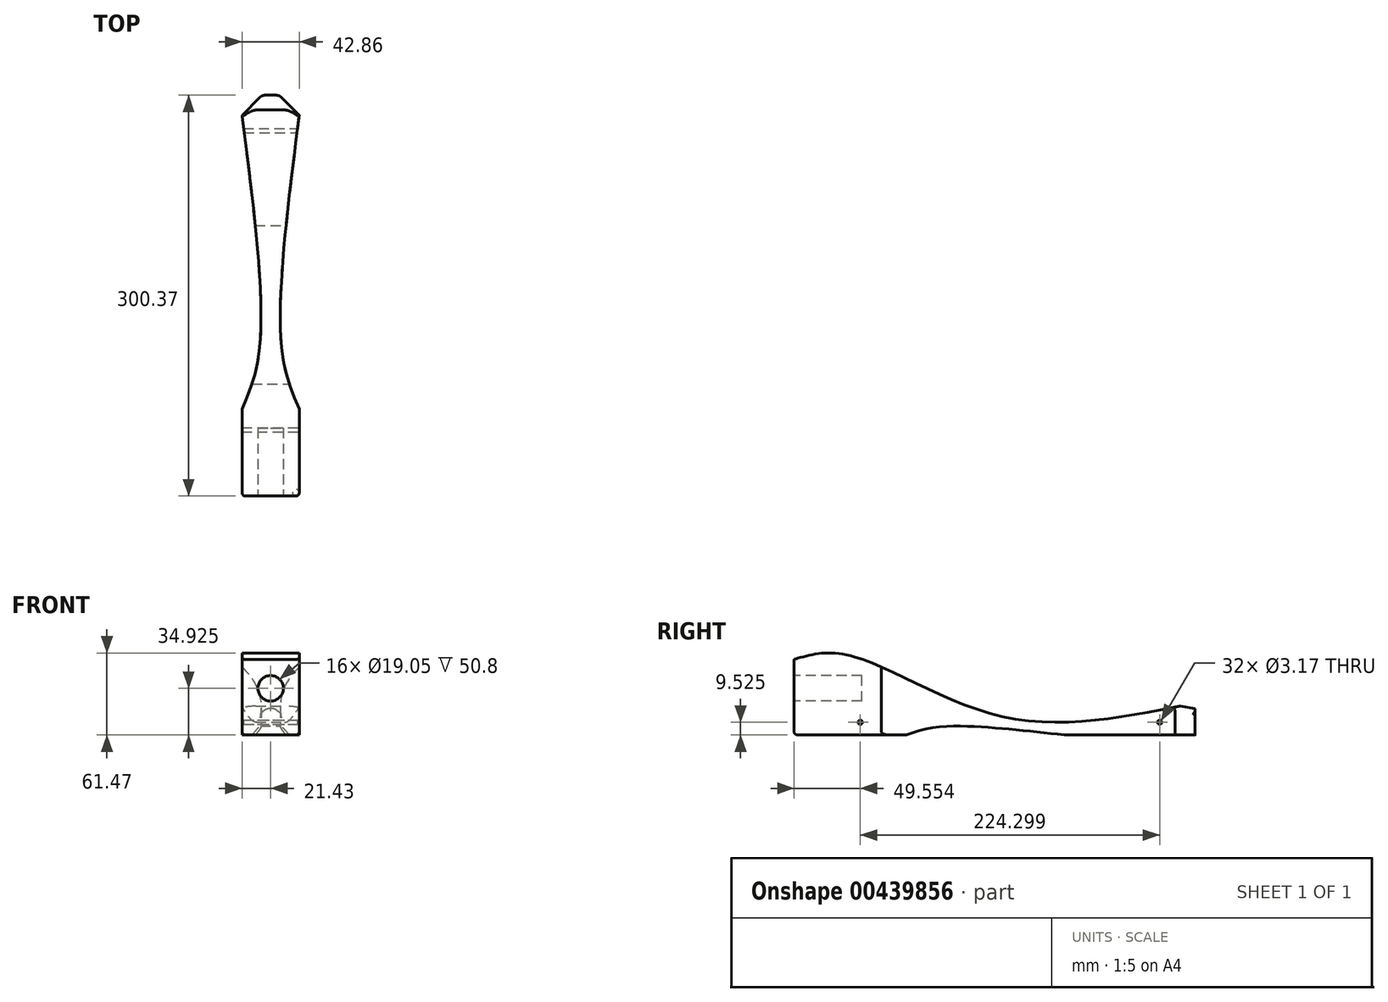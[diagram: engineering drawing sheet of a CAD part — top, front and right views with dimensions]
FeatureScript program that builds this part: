
annotation { "Feature Type Name" : "Feature", "Feature Type Description" : "" }
export const myFeature = defineFeature(function(context is Context, id is Id, definition is map)
    precondition{}
    {
        {
            var Q0;
            Q0=qCreatedBy(makeId("Right.planeOp"),FACE);
            var sketch = newSketch(context, id + "F0", { "sketchPlane" : qUnion([Q0])});
            skLineSegment(sketch, "E0", {"start": v(-152.4, 0) * mm, "end": v(152.4, 0) * mm});
            skLineSegment(sketch, "E1", {"start": v(-152.4, 0) * mm, "end": v(-152.4, 69.85) * mm});
            skLineSegment(sketch, "E2", {"start": v(152.4, 0) * mm, "end": v(152.4, 19.05) * mm});
            skLineSegment(sketch, "E3", {"start": v(152.4, 19.05) * mm, "end": v(-152.4, 69.85) * mm});
            skPoint(sketch, "E4.endSnap0", {"position": v(-152.4, 34.93) * mm});
            skLineSegment(sketch, "E5.0", {"start": v(-95.25, 50.8) * mm, "end": v(-152.4, 50.8) * mm, "construction": true});
            skLineSegment(sketch, "E5.1", {"start": v(-95.25, 50.8) * mm, "end": v(-95.25, 19.05) * mm, "construction": true});
            skLineSegment(sketch, "E5.2", {"start": v(-95.25, 19.05) * mm, "end": v(-152.4, 19.05) * mm, "construction": true});
            skSolve(sketch);
        }
        {
            var Q0;
            Q0=makeQuery(id+"F0.imprint","IMPRINT",FACE,{"disambiguationData":[TD([[makeQuery(id+"F0.imprint","IMPRINT",EDGE,{"derivedFrom":sQuery(id+"F0.wireOp",EDGE,"E0")}),1.0]])]});
            extrude(context, id + "F1", {"entities" : qUnion([Q0]), "depth" : 42.86 * mm, "symmetric" : true});
        }
        {
            var Q0;
            Q0=makeQuery(id+"F1.opExtrude","SWEPT_FACE",FACE,{"disambiguationData":[OSD([sQuery(id+"F0.wireOp",EDGE,"E1")])]});
            var sketch = newSketch(context, id + "F2", { "sketchPlane" : qUnion([Q0])});
            skLineSegment(sketch, "E6", {"start": v(21.43, 34.93) * mm, "end": v(0, 34.93) * mm, "construction": true});
            skCircle(sketch, "E7", {"center": v(0, 34.93) * mm, "radius": 9.53 * mm});
            skSolve(sketch);
        }
        {
            var Q0;
            Q0=makeQuery(id+"F2.imprint","IMPRINT",FACE,{"disambiguationData":[TD([[makeQuery(id+"F2.imprint","IMPRINT",EDGE,{"derivedFrom":sQuery(id+"F2.wireOp",EDGE,"E7")}),1.0]])]});
            var Q1;
            Q1=sQuery(id+"F2.wireOp",EDGE,"E7");
            extrude(context, id + "F3", {"entities" : qUnion([Q0]), "operationType" : NewBodyOperationType.REMOVE, "surfaceEntities" : qUnion([Q1]), "oppositeDirection" : true, "depth" : 50.8 * mm});
        }
        {
            var Q0;
            Q0=makeQuery(id+"F1.opExtrude","CAP_FACE",FACE,{"disambiguationData":[OSD([sQuery(id+"F0.wireOp",EDGE,"E0"),sQuery(id+"F0.wireOp",EDGE,"E1"),sQuery(id+"F0.wireOp",EDGE,"E2"),sQuery(id+"F0.wireOp",EDGE,"E3")])],"isStart":false});
            var sketch = newSketch(context, id + "F4", { "sketchPlane" : qUnion([Q0])});
            skLineSegment(sketch, "E8", {"start": v(-152.4, 34.93) * mm, "end": v(-152.4, 44.45) * mm, "construction": true});
            skLineSegment(sketch, "E9.0", {"start": v(-95.25, 19.05) * mm, "end": v(-152.4, 19.05) * mm, "construction": true});
            skLineSegment(sketch, "E9.1", {"start": v(-95.25, 50.8) * mm, "end": v(-95.25, 19.05) * mm, "construction": true});
            skLineSegment(sketch, "E9.2", {"start": v(-152.4, 50.8) * mm, "end": v(-95.25, 50.8) * mm, "construction": true});
            skLineSegment(sketch, "E10", {"start": v(57.15, 0) * mm, "end": v(57.15, 34.93) * mm, "construction": true});
            skLineSegment(sketch, "E11", {"start": v(-152.4, 44.45) * mm, "end": v(-101.6, 44.45) * mm, "construction": true});
            skLineSegment(sketch, "E12", {"start": v(-101.6, 44.45) * mm, "end": v(-101.6, 25.4) * mm, "construction": true});
            skLineSegment(sketch, "E13", {"start": v(-101.6, 25.4) * mm, "end": v(-152.4, 25.4) * mm, "construction": true});
            skFitSpline(sketch, "E14", {"points": [v(-152.4, 56.65) * mm, v(-111.85, 59.82) * mm, v(0, 14.63) * mm, v(136.83, 21.64) * mm], "startDerivative": vector(164.8, 47.68) * mm, "endDerivative": vector(342.19, 67.53) * mm});
            skLineSegment(sketch, "E15", {"start": v(-152.4, 56.65) * mm, "end": v(-152.4, 0) * mm});
            skLineSegment(sketch, "E16", {"start": v(-152.4, 0) * mm, "end": v(152.4, 0) * mm});
            skLineSegment(sketch, "E17", {"start": v(152.4, 0) * mm, "end": v(152.4, 19.05) * mm});
            skLineSegment(sketch, "E18", {"start": v(152.4, 19.05) * mm, "end": v(136.83, 21.64) * mm});
            skCircle(sketch, "E19", {"center": v(-102.85, 9.53) * mm, "radius": 1.59 * mm});
            skCircle(sketch, "E20", {"center": v(121.45, 9.53) * mm, "radius": 1.59 * mm});
            skFitSpline(sketch, "E21", {"points": [v(-68.4, 0) * mm, v(-42.6, 6.17) * mm, v(50.18, 0) * mm], "startDerivative": vector(62.26, 22.44) * mm, "endDerivative": vector(164.57, -18.32) * mm});
            skSolve(sketch);
        }
        {
            var Q0;
            Q0=makeQuery(id+"F1.opExtrude","SWEPT_FACE",FACE,{"disambiguationData":[OSD([sQuery(id+"F0.wireOp",EDGE,"E0")])]});
            var sketch = newSketch(context, id + "F5", { "sketchPlane" : qUnion([Q0])});
            skLineSegment(sketch, "E22", {"start": v(0, 152.4) * mm, "end": v(0, -152.4) * mm, "construction": true});
            skLineSegment(sketch, "E23", {"start": v(15.88, 152.4) * mm, "end": v(15.88, 95.25) * mm, "construction": true});
            skLineSegment(sketch, "E24", {"start": v(15.88, 95.25) * mm, "end": v(-15.87, 95.25) * mm, "construction": true});
            skLineSegment(sketch, "E25", {"start": v(-15.87, 95.25) * mm, "end": v(-15.87, 152.4) * mm, "construction": true});
            skLineSegment(sketch, "E26", {"start": v(0, 152.4) * mm, "end": v(-9.53, 152.4) * mm, "construction": true});
            skLineSegment(sketch, "E27", {"start": v(-9.53, 152.4) * mm, "end": v(-9.53, 101.6) * mm, "construction": true});
            skLineSegment(sketch, "E28", {"start": v(-9.52, 101.6) * mm, "end": v(9.53, 101.6) * mm, "construction": true});
            skLineSegment(sketch, "E29", {"start": v(9.53, 101.6) * mm, "end": v(9.53, 152.4) * mm, "construction": true});
            skLineSegment(sketch, "E30", {"start": v(0, -147.97) * mm, "end": v(-6.45, -147.97) * mm});
            skLineSegment(sketch, "E31", {"start": v(-6.45, -147.97) * mm, "end": v(-21.43, -132.9) * mm});
            skLineSegment(sketch, "E32.MirrorCS", {"start": v(0, -147.97) * mm, "end": v(6.45, -147.97) * mm});
            skLineSegment(sketch, "E33.MirrorCS", {"start": v(6.45, -147.97) * mm, "end": v(21.43, -132.9) * mm});
            skLineSegment(sketch, "E34", {"start": v(-21.43, -132.9) * mm, "end": v(-21.43, -152.4) * mm});
            skLineSegment(sketch, "E35", {"start": v(-21.43, -152.4) * mm, "end": v(21.43, -152.4) * mm});
            skLineSegment(sketch, "E36", {"start": v(21.43, -152.4) * mm, "end": v(21.43, -132.9) * mm});
            skLineSegment(sketch, "E37", {"start": v(-6.45, -147.97) * mm, "end": v(6.45, -147.97) * mm});
            skLineSegment(sketch, "E38", {"start": v(21.43, -132.9) * mm, "end": v(21.43, 152.4) * mm});
            skLineSegment(sketch, "E39", {"start": v(21.43, 152.4) * mm, "end": v(-21.43, 152.4) * mm});
            skLineSegment(sketch, "E40", {"start": v(-21.43, 152.4) * mm, "end": v(-21.43, -132.9) * mm});
            skFitSpline(sketch, "E41", {"points": [v(-21.43, 87.09) * mm, v(-8.22, 41.22) * mm, v(-21.43, -132.9) * mm], "startDerivative": vector(48.54, -111.02) * mm, "endDerivative": vector(-39.36, -308.36) * mm});
            skFitSpline(sketch, "E42.MirrorCS", {"points": [v(21.43, 87.09) * mm, v(8.22, 41.22) * mm, v(21.43, -132.9) * mm], "startDerivative": vector(-48.54, -111.02) * mm, "endDerivative": vector(39.36, -308.36) * mm});
            skSolve(sketch);
        }
        {
            var Q0;
            Q0=makeQuery(id+"F4.imprint","IMPRINT",FACE,{"disambiguationData":[TD([[makeQuery(id+"F4.imprint","IMPRINT",EDGE,{"derivedFrom":sQuery(id+"F4.wireOp",EDGE,"E14")}),-1.0]])]});
            extrude(context, id + "F6", {"entities" : qUnion([Q0]), "operationType" : NewBodyOperationType.INTERSECT, "endBound" : BoundingType.THROUGH_ALL, "oppositeDirection" : true, "depth" : 25.4 * mm});
        }
        {
            var Q0;
            Q0=makeQuery(id+"F5.imprint","IMPRINT",FACE,{"disambiguationData":[TD([[makeQuery(id+"F5.imprint","IMPRINT",EDGE,{"derivedFrom":sQuery(id+"F5.wireOp",EDGE,"E31")}),1.0]])]});
            extrude(context, id + "F7", {"entities" : qUnion([Q0]), "operationType" : NewBodyOperationType.REMOVE, "oppositeDirection" : true, "depth" : 25.4 * mm});
        }
        {
            var Q0;
            Q0=makeQuery(id+"F5.imprint","IMPRINT",FACE,{"disambiguationData":[TD([[makeQuery(id+"F5.imprint","IMPRINT",EDGE,{"derivedFrom":sQuery(id+"F5.wireOp",EDGE,"E31")}),-1.0]])]});
            extrude(context, id + "F8", {"entities" : qUnion([Q0]), "operationType" : NewBodyOperationType.INTERSECT, "endBound" : BoundingType.THROUGH_ALL, "oppositeDirection" : true, "depth" : 25.4 * mm});
        }
        {
            var Q0;
            Q0=makeQuery(id+"F7.boolean.opBoolean","INTERSECT",EDGE,{"derivedFrom":[makeQuery(id+"F1.opExtrude","SWEPT_FACE",FACE,{"disambiguationData":[OSD([sQuery(id+"F0.wireOp",EDGE,"E3")])]}),makeQuery(id+"F7.opExtrude","SWEPT_FACE",FACE,{"disambiguationData":[OSD([sQuery(id+"F5.wireOp",EDGE,"E31")])]})]});
            var Q1;
            Q1=makeQuery(id+"F7.boolean.opBoolean","INTERSECT",EDGE,{"derivedFrom":[makeQuery(id+"F1.opExtrude","SWEPT_FACE",FACE,{"disambiguationData":[OSD([sQuery(id+"F0.wireOp",EDGE,"E3")])]}),makeQuery(id+"F7.opExtrude","SWEPT_FACE",FACE,{"disambiguationData":[OSD([sQuery(id+"F5.wireOp",EDGE,"E33.MirrorCS")])]})]});
            var Q2;
            Q2=makeQuery(id+"F7.boolean.opBoolean","COPY",EDGE,{"derivedFrom":makeQuery(id+"F7.opExtrude","SWEPT_EDGE",EDGE,{"disambiguationData":[OSD([sQuery(id+"F5.wireOp",EDGE,"E31"),sQuery(id+"F5.wireOp",EDGE,"E37")])]})});
            var Q3;
            Q3=makeQuery(id+"F7.boolean.opBoolean","COPY",EDGE,{"derivedFrom":makeQuery(id+"F7.opExtrude","SWEPT_EDGE",EDGE,{"disambiguationData":[OSD([sQuery(id+"F5.wireOp",EDGE,"E33.MirrorCS"),sQuery(id+"F5.wireOp",EDGE,"E37")])]})});
            var Q4;
            {var subQ0=sQuery(id+"F5.wireOp",EDGE,"E42.MirrorCS");var subQ1=sQuery(id+"F5.wireOp",EDGE,"E38");var subQ2=sQuery(id+"F5.wireOp",EDGE,"E36");var subQ3=sQuery(id+"F5.wireOp",EDGE,"E33.MirrorCS");Q4=makeQuery(id+"F8.boolean.opBoolean","MERGE",EDGE,{"derivedFrom":[makeQuery(id+"F7.boolean.opBoolean","COPY",EDGE,{"derivedFrom":makeQuery(id+"F7.opExtrude","SWEPT_EDGE",EDGE,{"disambiguationData":[OSD([subQ3,subQ2,subQ1,subQ0])]})}),makeQuery(id+"F8.boolean.toolComplement.opBoolean","COPY",EDGE,{"derivedFrom":makeQuery(id+"F8.opExtrude","SWEPT_EDGE",EDGE,{"disambiguationData":[OSD([subQ3,subQ2,subQ1,subQ0])]})})]});}
            var Q5;
            Q5=makeQuery(id+"F7.boolean.opBoolean","COPY",EDGE,{"derivedFrom":makeQuery(id+"F7.opExtrude","CAP_EDGE",EDGE,{"disambiguationData":[OSD([sQuery(id+"F5.wireOp",EDGE,"E33.MirrorCS")])],"isStart":true})});
            var Q6;
            Q6=makeQuery(id+"F7.boolean.opBoolean","COPY",EDGE,{"derivedFrom":makeQuery(id+"F7.opExtrude","CAP_EDGE",EDGE,{"disambiguationData":[OSD([sQuery(id+"F5.wireOp",EDGE,"E37")])],"isStart":true})});
            var Q7;
            Q7=makeQuery(id+"F7.boolean.opBoolean","COPY",EDGE,{"derivedFrom":makeQuery(id+"F7.opExtrude","CAP_EDGE",EDGE,{"disambiguationData":[OSD([sQuery(id+"F5.wireOp",EDGE,"E31")])],"isStart":true})});
            var Q8;
            {var subQ0=sQuery(id+"F5.wireOp",EDGE,"E41");var subQ1=sQuery(id+"F5.wireOp",EDGE,"E40");var subQ2=sQuery(id+"F5.wireOp",EDGE,"E34");var subQ3=sQuery(id+"F5.wireOp",EDGE,"E31");Q8=makeQuery(id+"F8.boolean.opBoolean","MERGE",EDGE,{"derivedFrom":[makeQuery(id+"F7.boolean.opBoolean","COPY",EDGE,{"derivedFrom":makeQuery(id+"F7.opExtrude","SWEPT_EDGE",EDGE,{"disambiguationData":[OSD([subQ3,subQ2,subQ1,subQ0])]})}),makeQuery(id+"F8.boolean.toolComplement.opBoolean","COPY",EDGE,{"derivedFrom":makeQuery(id+"F8.opExtrude","SWEPT_EDGE",EDGE,{"disambiguationData":[OSD([subQ3,subQ2,subQ1,subQ0])]})})]});}
            fillet(context, id + "F9", {"entities" : qUnion([Q0, Q1, Q2, Q3, Q4, Q5, Q6, Q7, Q8]), "radius" : 5.08 * mm, "tangentPropagation" : true, "allowEdgeOverflow" : false});
        }
        {
            var Q0;
            Q0=makeQuery(id+"F8.boolean.opBoolean","INTERSECT",EDGE,{"derivedFrom":[makeQuery(id+"F6.boolean.opBoolean","COPY",FACE,{"derivedFrom":makeQuery(id+"F6.boolean.toolComplement.opBoolean","COPY",FACE,{"derivedFrom":makeQuery(id+"F6.opExtrude","SWEPT_FACE",FACE,{"disambiguationData":[OSD([sQuery(id+"F4.wireOp",EDGE,"E14")])]})})}),makeQuery(id+"F8.boolean.toolComplement.opBoolean","COPY",FACE,{"derivedFrom":makeQuery(id+"F8.opExtrude","SWEPT_FACE",FACE,{"disambiguationData":[OSD([sQuery(id+"F5.wireOp",EDGE,"E41")])]})})]});
            var Q1;
            Q1=makeQuery(id+"F8.boolean.opBoolean","INTERSECT",EDGE,{"derivedFrom":[makeQuery(id+"F6.boolean.opBoolean","COPY",FACE,{"derivedFrom":makeQuery(id+"F6.boolean.toolComplement.opBoolean","COPY",FACE,{"derivedFrom":makeQuery(id+"F6.opExtrude","SWEPT_FACE",FACE,{"disambiguationData":[OSD([sQuery(id+"F4.wireOp",EDGE,"E14")])]})})}),makeQuery(id+"F8.boolean.toolComplement.opBoolean","COPY",FACE,{"derivedFrom":makeQuery(id+"F8.opExtrude","SWEPT_FACE",FACE,{"disambiguationData":[OSD([sQuery(id+"F5.wireOp",EDGE,"E42.MirrorCS")])]})})]});
            var Q2;
            Q2=makeQuery(id+"F6.boolean.opBoolean","INTERSECT",EDGE,{"derivedFrom":[makeQuery(id+"F1.opExtrude","CAP_FACE",FACE,{"disambiguationData":[OSD([sQuery(id+"F0.wireOp",EDGE,"E0"),sQuery(id+"F0.wireOp",EDGE,"E1"),sQuery(id+"F0.wireOp",EDGE,"E2"),sQuery(id+"F0.wireOp",EDGE,"E3")])],"isStart":true}),makeQuery(id+"F6.boolean.toolComplement.opBoolean","COPY",FACE,{"derivedFrom":makeQuery(id+"F6.opExtrude","SWEPT_FACE",FACE,{"disambiguationData":[OSD([sQuery(id+"F4.wireOp",EDGE,"E14")])]})})]});
            var Q3;
            Q3=makeQuery(id+"F6.boolean.opBoolean","COPY",EDGE,{"derivedFrom":makeQuery(id+"F6.boolean.toolComplement.opBoolean","COPY",EDGE,{"derivedFrom":makeQuery(id+"F6.opExtrude","CAP_EDGE",EDGE,{"disambiguationData":[OSD([sQuery(id+"F4.wireOp",EDGE,"E14")])],"isStart":true})})});
            var Q4;
            Q4=makeQuery(id+"F1.opExtrude","CAP_EDGE",EDGE,{"disambiguationData":[OSD([sQuery(id+"F0.wireOp",EDGE,"E0")])],"isStart":false});
            var Q5;
            Q5=makeQuery(id+"F8.boolean.opBoolean","COPY",EDGE,{"derivedFrom":makeQuery(id+"F8.boolean.toolComplement.opBoolean","COPY",EDGE,{"derivedFrom":makeQuery(id+"F8.opExtrude","CAP_EDGE",EDGE,{"disambiguationData":[OSD([sQuery(id+"F5.wireOp",EDGE,"E42.MirrorCS")])],"isStart":true})})});
            var Q6;
            Q6=makeQuery(id+"F1.opExtrude","CAP_EDGE",EDGE,{"disambiguationData":[OSD([sQuery(id+"F0.wireOp",EDGE,"E1")])],"isStart":true});
            var Q7;
            Q7=makeQuery(id+"F1.opExtrude","CAP_EDGE",EDGE,{"disambiguationData":[OSD([sQuery(id+"F0.wireOp",EDGE,"E1")])],"isStart":false});
            var Q8;
            Q8=makeQuery(id+"F1.opExtrude","SWEPT_EDGE",EDGE,{"disambiguationData":[OSD([sQuery(id+"F0.wireOp",EDGE,"E0"),sQuery(id+"F0.wireOp",EDGE,"E1")])]});
            var Q9;
            Q9=makeQuery(id+"F6.boolean.opBoolean","COPY",EDGE,{"derivedFrom":makeQuery(id+"F6.boolean.toolComplement.opBoolean","COPY",EDGE,{"derivedFrom":makeQuery(id+"F6.opExtrude","SWEPT_EDGE",EDGE,{"disambiguationData":[OSD([sQuery(id+"F0.wireOp",EDGE,"E1"),sQuery(id+"F4.wireOp",EDGE,"E14"),sQuery(id+"F4.wireOp",EDGE,"E15")])]})})});
            var Q10;
            Q10=makeQuery(id+"F1.opExtrude","CAP_EDGE",EDGE,{"disambiguationData":[OSD([sQuery(id+"F0.wireOp",EDGE,"E0")])],"isStart":true});
            var Q11;
            Q11=makeQuery(id+"F8.boolean.opBoolean","COPY",EDGE,{"derivedFrom":makeQuery(id+"F8.boolean.toolComplement.opBoolean","COPY",EDGE,{"derivedFrom":makeQuery(id+"F8.opExtrude","CAP_EDGE",EDGE,{"disambiguationData":[OSD([sQuery(id+"F5.wireOp",EDGE,"E41")])],"isStart":true})})});
            var Q12;
            Q12=makeQuery(id+"F8.boolean.opBoolean","INTERSECT",EDGE,{"derivedFrom":[makeQuery(id+"F6.boolean.opBoolean","COPY",FACE,{"derivedFrom":makeQuery(id+"F6.boolean.toolComplement.opBoolean","COPY",FACE,{"derivedFrom":makeQuery(id+"F6.opExtrude","SWEPT_FACE",FACE,{"disambiguationData":[OSD([sQuery(id+"F4.wireOp",EDGE,"E21")])]})})}),makeQuery(id+"F8.boolean.toolComplement.opBoolean","COPY",FACE,{"derivedFrom":makeQuery(id+"F8.opExtrude","SWEPT_FACE",FACE,{"disambiguationData":[OSD([sQuery(id+"F5.wireOp",EDGE,"E42.MirrorCS")])]})})]});
            var Q13;
            Q13=makeQuery(id+"F8.boolean.opBoolean","INTERSECT",EDGE,{"derivedFrom":[makeQuery(id+"F6.boolean.opBoolean","COPY",FACE,{"derivedFrom":makeQuery(id+"F6.boolean.toolComplement.opBoolean","COPY",FACE,{"derivedFrom":makeQuery(id+"F6.opExtrude","SWEPT_FACE",FACE,{"disambiguationData":[OSD([sQuery(id+"F4.wireOp",EDGE,"E21")])]})})}),makeQuery(id+"F8.boolean.toolComplement.opBoolean","COPY",FACE,{"derivedFrom":makeQuery(id+"F8.opExtrude","SWEPT_FACE",FACE,{"disambiguationData":[OSD([sQuery(id+"F5.wireOp",EDGE,"E41")])]})})]});
            var Q14;
            Q14=makeQuery(id+"F8.boolean.opBoolean","COPY",EDGE,{"derivedFrom":makeQuery(id+"F8.boolean.toolComplement.opBoolean","COPY",EDGE,{"derivedFrom":makeQuery(id+"F8.opExtrude","SWEPT_EDGE",EDGE,{"disambiguationData":[OSD([sQuery(id+"F5.wireOp",EDGE,"E38"),sQuery(id+"F5.wireOp",EDGE,"E42.MirrorCS")])]})})});
            var Q15;
            Q15=makeQuery(id+"F8.boolean.opBoolean","COPY",EDGE,{"derivedFrom":makeQuery(id+"F8.boolean.toolComplement.opBoolean","COPY",EDGE,{"derivedFrom":makeQuery(id+"F8.opExtrude","SWEPT_EDGE",EDGE,{"disambiguationData":[OSD([sQuery(id+"F5.wireOp",EDGE,"E40"),sQuery(id+"F5.wireOp",EDGE,"E41")])]})})});
            fillet(context, id + "F10", {"entities" : qUnion([Q0, Q1, Q2, Q3, Q4, Q5, Q6, Q7, Q8, Q9, Q10, Q11, Q12, Q13, Q14, Q15]), "radius" : 2.54 * mm, "tangentPropagation" : true, "allowEdgeOverflow" : false});
        }
    });
